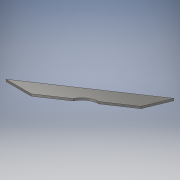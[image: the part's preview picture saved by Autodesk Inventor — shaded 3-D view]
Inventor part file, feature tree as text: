
AUTODESK INVENTOR PART (.ipt)
format: ipt  version: 2018 (Build 220112000, 112)  size: 112,128 bytes
history: native  units: in
note: dims shown in document units (in); Inventor stores cm internally (conversion verified against a paired STEP export)
features: extrude x1, sketch x1
ambient origin geometry x8: Origin, YZ Plane, XZ Plane, XY Plane, X Axis, Y Axis, Z Axis, Center Point
bodies: Solid1 (feature_tree)
feature tree (2):
  extrude  "Extrusion1"  Depth=1.125in
  sketch  "Sketch1"  dims[d0=0.7719in d2=1.56in d3=1.75in d4=1.75in d5=1.5in d6=1.5in d7=0.7719in d8=0.125in d9=0.0in d10=0.5in d12=0.5in d13=1.125in]
